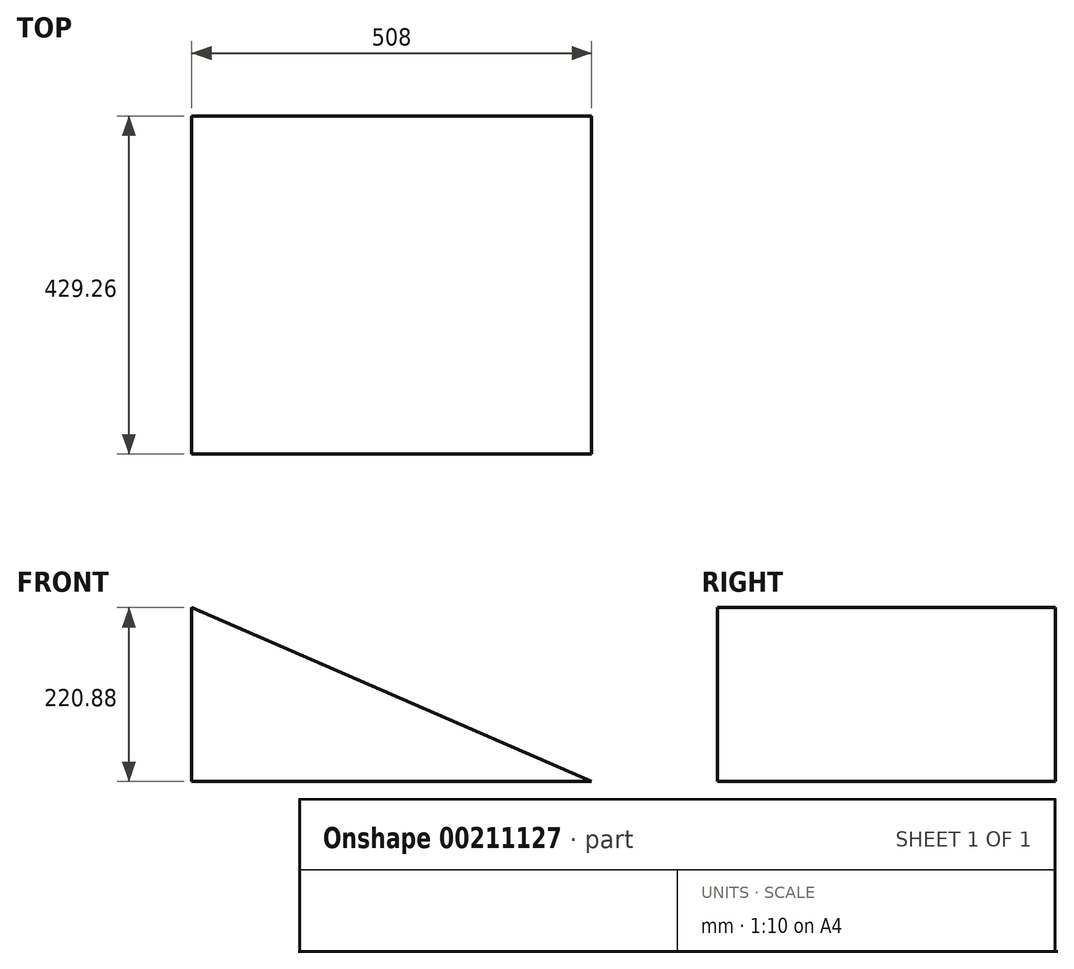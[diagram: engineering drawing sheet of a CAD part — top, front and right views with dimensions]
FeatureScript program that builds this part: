
annotation { "Feature Type Name" : "Feature", "Feature Type Description" : "" }
export const myFeature = defineFeature(function(context is Context, id is Id, definition is map)
    precondition{}
    {
        {
            var Q0;
            Q0=qCreatedBy(makeId("Front.planeOp"),FACE);
            var sketch = newSketch(context, id + "F0", { "sketchPlane" : qUnion([Q0])});
            skLineSegment(sketch, "E0", {"start": v(0, 0) * mm, "end": v(0, 220.88) * mm});
            skLineSegment(sketch, "E1", {"start": v(0, 220.88) * mm, "end": v(508, 0) * mm});
            skLineSegment(sketch, "E2", {"start": v(508, 0) * mm, "end": v(0, 0) * mm});
            skSolve(sketch);
        }
        {
            var Q0;
            Q0 = qSketchRegion(id + "F0", true);
            extrude(context, id + "F1", {"entities" : qUnion([Q0]), "depth" : 429.26 * mm});
        }
    });
